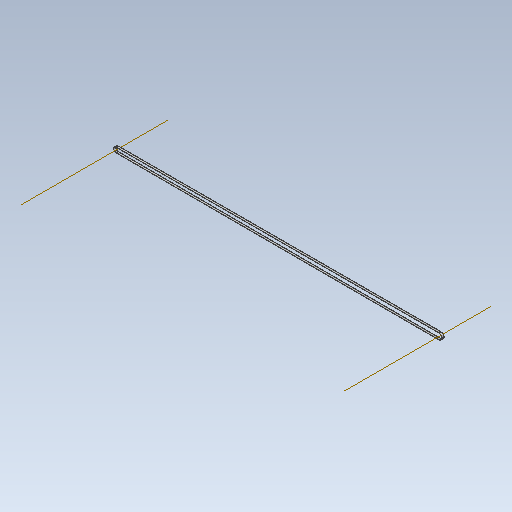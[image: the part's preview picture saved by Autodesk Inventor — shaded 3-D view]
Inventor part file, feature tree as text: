
AUTODESK INVENTOR PART (.ipt)
format: ipt  version: 2020 (Build 240168000, 168)  size: 92,160 bytes
history: native  units: mm (DEFAULTED — no unit token found)
features: other x4, plane x2, sketch x1, sweep x1
ambient origin geometry x8: Origin, YZ Plane, XZ Plane, XY Plane, X Axis, Y Axis, Z Axis, Center Point
bodies: Solid1 (feature_tree)
feature tree (8):
  sketch  "Sketch Path"  dims[d0=4.0mm d2=0.0mm d4=0.3mm d5=0.3mm d6=0.0mm d7=0.0mm d8=0.0mm d9=0.0mm d10=0.0mm d11=0.0mm]
  other  "Cross Section Plane"
  other  "Work Axis1"
  other  "Work Axis2"
  plane  "Work Plane2"
  plane  "Work Plane3"
  sweep  "Belt"
  other  "Cross Section"
